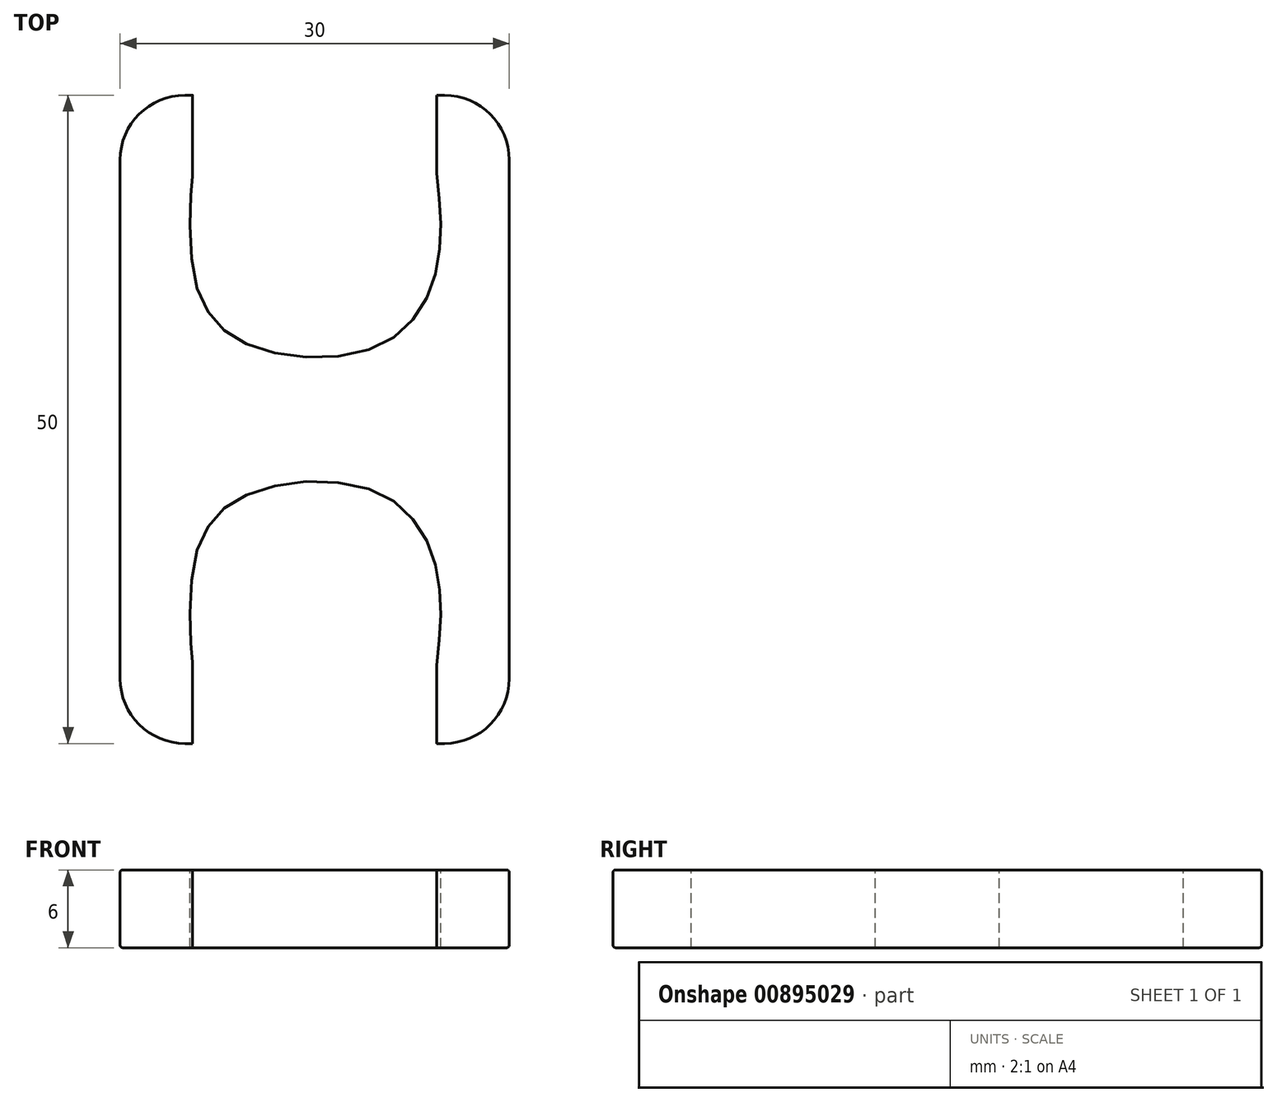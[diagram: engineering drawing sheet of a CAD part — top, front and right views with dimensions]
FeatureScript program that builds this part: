
annotation { "Feature Type Name" : "Feature", "Feature Type Description" : "" }
export const myFeature = defineFeature(function(context is Context, id is Id, definition is map)
    precondition{}
    {
        {
            var Q0;
            Q0=qCreatedBy(makeId("Top.planeOp"),FACE);
            var sketch = newSketch(context, id + "F0", { "sketchPlane" : qUnion([Q0])});
            skLineSegment(sketch, "E0.bottom", {"start": v(15, 25) * mm, "end": v(-15, 25) * mm});
            skLineSegment(sketch, "E0.top", {"start": v(15, -25) * mm, "end": v(-15, -25) * mm});
            skLineSegment(sketch, "E0.left", {"start": v(15, 25) * mm, "end": v(15, -25) * mm});
            skLineSegment(sketch, "E0.right", {"start": v(-15, 25) * mm, "end": v(-15, -25) * mm});
            skPoint(sketch, "E0.middle", {"position": v(0, 0) * mm});
            skSolve(sketch);
        }
        {
            var Q0;
            Q0 = qSketchRegion(id + "F0", true);
            extrude(context, id + "F1", {"entities" : qUnion([Q0]), "depth" : 6 * mm, "offsetDistance" : 25 * mm});
        }
        {
            var Q0;
            Q0=makeQuery(id+"F1.opExtrude","SWEPT_EDGE",EDGE,{"disambiguationData":[OSD([sQuery(id+"F0.wireOp",EDGE,"E0.bottom"),sQuery(id+"F0.wireOp",EDGE,"E0.right")])]});
            var Q1;
            Q1=makeQuery(id+"F1.opExtrude","SWEPT_EDGE",EDGE,{"disambiguationData":[OSD([sQuery(id+"F0.wireOp",EDGE,"E0.bottom"),sQuery(id+"F0.wireOp",EDGE,"E0.left")])]});
            var Q2;
            Q2=makeQuery(id+"F1.opExtrude","SWEPT_EDGE",EDGE,{"disambiguationData":[OSD([sQuery(id+"F0.wireOp",EDGE,"E0.top"),sQuery(id+"F0.wireOp",EDGE,"E0.right")])]});
            var Q3;
            Q3=makeQuery(id+"F1.opExtrude","SWEPT_EDGE",EDGE,{"disambiguationData":[OSD([sQuery(id+"F0.wireOp",EDGE,"E0.top"),sQuery(id+"F0.wireOp",EDGE,"E0.left")])]});
            fillet(context, id + "F2", {"entities" : qUnion([Q0, Q1, Q2, Q3]), "radius" : 5 * mm, "tangentPropagation" : true, "allowEdgeOverflow" : false});
        }
        {
            var Q0;
            Q0=makeQuery(id+"F1.opExtrude","CAP_FACE",FACE,{"disambiguationData":[OSD([sQuery(id+"F0.wireOp",EDGE,"E0.bottom"),sQuery(id+"F0.wireOp",EDGE,"E0.top"),sQuery(id+"F0.wireOp",EDGE,"E0.left"),sQuery(id+"F0.wireOp",EDGE,"E0.right")])],"isStart":false});
            var Q1;
            Q1=makeQuery(id+"F1.opExtrude","CAP_FACE",FACE,{"disambiguationData":[OSD([sQuery(id+"F0.wireOp",EDGE,"E0.bottom"),sQuery(id+"F0.wireOp",EDGE,"E0.top"),sQuery(id+"F0.wireOp",EDGE,"E0.left"),sQuery(id+"F0.wireOp",EDGE,"E0.right")])],"isStart":true});
            fillet(context, id + "F3", {"entities" : qUnion([Q0, Q1]), "radius" : 0.2 * mm, "tangentPropagation" : true, "allowEdgeOverflow" : false});
        }
        {
            var Q0;
            Q0=makeQuery(id+"F1.opExtrude","CAP_FACE",FACE,{"disambiguationData":[OSD([sQuery(id+"F0.wireOp",EDGE,"E0.bottom"),sQuery(id+"F0.wireOp",EDGE,"E0.top"),sQuery(id+"F0.wireOp",EDGE,"E0.left"),sQuery(id+"F0.wireOp",EDGE,"E0.right")])],"isStart":false});
            var sketch = newSketch(context, id + "F4", { "sketchPlane" : qUnion([Q0])});
            skFitSpline(sketch, "E1", {"points": [v(9.41, 18.98) * mm, v(9.41, 11.7) * mm, v(5.2, 5.8) * mm, v(-5.2, 5.8) * mm, v(-9.41, 11.7) * mm, v(-9.41, 18.97) * mm, v(-9.41, 18.98) * mm, v(-9.41, 18.98) * mm, v(-9.41, 20.48) * mm, v(-9.41, 21.99) * mm]});
            skFitSpline(sketch, "E2", {"points": [v(-9.41, 21.99) * mm, v(-9.41, 23.45) * mm, v(-9.41, 24.92) * mm, v(-9.41, 25) * mm, v(-9.41, 25) * mm, v(-9.41, 25) * mm]});
            skFitSpline(sketch, "E3", {"points": [v(-9.41, 25) * mm, v(-9.41, 25) * mm, v(-9.41, 25) * mm, v(-9.17, 25) * mm, v(9.17, 25) * mm, v(9.41, 25) * mm, v(9.41, 25) * mm, v(9.41, 25) * mm]});
            skFitSpline(sketch, "E4", {"points": [v(9.41, 25) * mm, v(9.41, 25) * mm, v(9.41, 25) * mm, v(9.41, 24.85) * mm, v(9.41, 19.13) * mm, v(9.41, 18.98) * mm, v(9.41, 18.98) * mm, v(9.41, 18.98) * mm]});
            skLineSegment(sketch, "E5", {"start": v(-9.41, 25) * mm, "end": v(9.41, 25) * mm});
            skFitSpline(sketch, "E6.MirrorCS", {"points": [v(-9.41, -25) * mm, v(-9.41, -25) * mm, v(-9.41, -25) * mm, v(-9.17, -25) * mm, v(9.17, -25) * mm, v(9.41, -25) * mm, v(9.41, -25) * mm, v(9.41, -25) * mm]});
            skFitSpline(sketch, "E7.MirrorCS", {"points": [v(-9.41, -21.99) * mm, v(-9.41, -23.45) * mm, v(-9.41, -24.92) * mm, v(-9.41, -25) * mm, v(-9.41, -25) * mm, v(-9.41, -25) * mm]});
            skFitSpline(sketch, "E8.MirrorCS", {"points": [v(9.41, -18.98) * mm, v(9.41, -11.7) * mm, v(5.2, -5.8) * mm, v(-5.2, -5.8) * mm, v(-9.41, -11.7) * mm, v(-9.41, -18.97) * mm, v(-9.41, -18.98) * mm, v(-9.41, -18.98) * mm, v(-9.41, -20.48) * mm, v(-9.41, -21.99) * mm]});
            skFitSpline(sketch, "E9.MirrorCS", {"points": [v(9.41, -25) * mm, v(9.41, -25) * mm, v(9.41, -25) * mm, v(9.41, -24.85) * mm, v(9.41, -19.13) * mm, v(9.41, -18.98) * mm, v(9.41, -18.98) * mm, v(9.41, -18.98) * mm]});
            skSolve(sketch);
        }
        {
            var Q0;
            Q0 = qSketchRegion(id + "F4", true);
            extrude(context, id + "F5", {"entities" : qUnion([Q0]), "operationType" : NewBodyOperationType.REMOVE, "oppositeDirection" : true, "depth" : 25 * mm, "offsetDistance" : 25 * mm});
        }
    });
